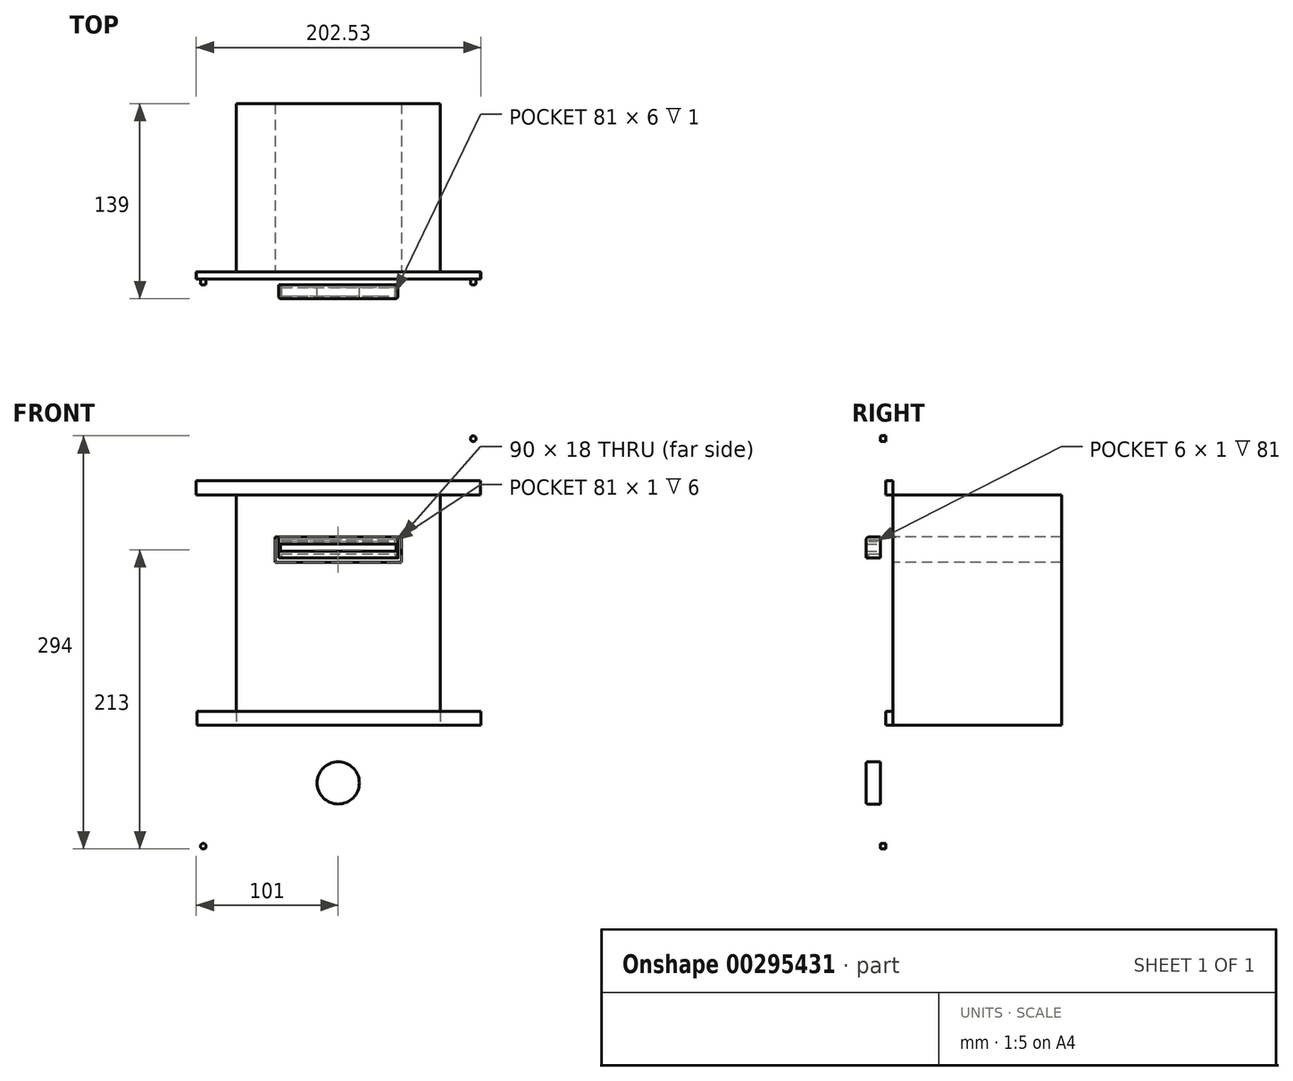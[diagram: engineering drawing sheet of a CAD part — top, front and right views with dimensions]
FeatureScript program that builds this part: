
annotation { "Feature Type Name" : "Feature", "Feature Type Description" : "" }
export const myFeature = defineFeature(function(context is Context, id is Id, definition is map)
    precondition{}
    {
        {
            var Q0;
            Q0=qCreatedBy(makeId("Front.planeOp"),FACE);
            var sketch = newSketch(context, id + "F0", { "sketchPlane" : qUnion([Q0])});
            skLineSegment(sketch, "E0.bottom", {"start": v(-143.29, 262) * mm, "end": v(58.71, 262) * mm});
            skLineSegment(sketch, "E0.top", {"start": v(-143.29, -38) * mm, "end": v(58.71, -38) * mm});
            skLineSegment(sketch, "E0.left", {"start": v(-143.29, 262) * mm, "end": v(-143.29, -38) * mm});
            skLineSegment(sketch, "E0.right", {"start": v(58.71, 262) * mm, "end": v(58.71, -38) * mm});
            skSolve(sketch);
        }
        {
            var Q0;
            Q0=makeQuery(id+"F0.imprint","IMPRINT",FACE,{"disambiguationData":[TD([[makeQuery(id+"F0.imprint","IMPRINT",EDGE,{"derivedFrom":sQuery(id+"F0.wireOp",EDGE,"E0.bottom")}),-1.0]])]});
            extrude(context, id + "F1", {"entities" : qUnion([Q0]), "depth" : 4 * mm});
        }
        {
            var Q0;
            Q0=makeQuery(id+"F1.opExtrude","CAP_FACE",FACE,{"disambiguationData":[OSD([sQuery(id+"F0.wireOp",EDGE,"E0.bottom"),sQuery(id+"F0.wireOp",EDGE,"E0.top"),sQuery(id+"F0.wireOp",EDGE,"E0.left"),sQuery(id+"F0.wireOp",EDGE,"E0.right")])],"isStart":false});
            var sketch = newSketch(context, id + "F2", { "sketchPlane" : qUnion([Q0])});
            skCircle(sketch, "E1", {"center": v(-138.29, 257) * mm, "radius": 2 * mm});
            skLineSegment(sketch, "E2", {"start": v(-143.29, 262) * mm, "end": v(-143.29, -38) * mm, "construction": true});
            skLineSegment(sketch, "E3", {"start": v(-143.29, 112) * mm, "end": v(-42.29, 112) * mm, "construction": true});
            skLineSegment(sketch, "E4", {"start": v(-42.29, 112) * mm, "end": v(-42.29, 262) * mm, "construction": true});
            skCircle(sketch, "E5.MirrorC", {"center": v(-138.29, -33) * mm, "radius": 2 * mm});
            skLineSegment(sketch, "E6.bottom", {"start": v(-83.29, 182) * mm, "end": v(-1.29, 182) * mm});
            skLineSegment(sketch, "E6.top", {"start": v(-83.29, 177) * mm, "end": v(-1.29, 177) * mm});
            skLineSegment(sketch, "E6.left", {"start": v(-83.29, 182) * mm, "end": v(-83.29, 177) * mm});
            skLineSegment(sketch, "E6.right", {"start": v(-1.29, 182) * mm, "end": v(-1.29, 177) * mm});
            skCircle(sketch, "E7.MirrorC", {"center": v(53.71, 257) * mm, "radius": 2 * mm});
            skCircle(sketch, "E8.MirrorC", {"center": v(53.71, -33) * mm, "radius": 2 * mm});
            skSolve(sketch);
        }
        {
            var Q0;
            Q0=makeQuery(id+"F2.imprint","IMPRINT",FACE,{"disambiguationData":[TD([[makeQuery(id+"F2.imprint","IMPRINT",EDGE,{"derivedFrom":sQuery(id+"F2.wireOp",EDGE,"f3714297-d91a-48a6-a239-89a6e6a1d6ad0.MirrorC")}),1.0]])]});
            var Q1;
            Q1=makeQuery(id+"F2.imprint","IMPRINT",FACE,{"disambiguationData":[TD([[makeQuery(id+"F2.imprint","IMPRINT",EDGE,{"derivedFrom":sQuery(id+"F2.wireOp",EDGE,"E5.MirrorC")}),-1.0]])]});
            var Q2;
            Q2=makeQuery(id+"F2.imprint","IMPRINT",FACE,{"disambiguationData":[TD([[makeQuery(id+"F2.imprint","IMPRINT",EDGE,{"derivedFrom":sQuery(id+"F2.wireOp",EDGE,"8d8d8ab8-7da3-4b74-95fe-22b7e39185220.MirrorC")}),-1.0]])]});
            var Q3;
            Q3=makeQuery(id+"F2.imprint","IMPRINT",FACE,{"disambiguationData":[TD([[makeQuery(id+"F2.imprint","IMPRINT",EDGE,{"derivedFrom":sQuery(id+"F2.wireOp",EDGE,"E1")}),1.0]])]});
            var Q4;
            Q4=makeQuery(id+"F2.imprint","IMPRINT",FACE,{"disambiguationData":[TD([[makeQuery(id+"F2.imprint","IMPRINT",EDGE,{"derivedFrom":sQuery(id+"F2.wireOp",EDGE,"E7.MirrorC")}),-1.0]])]});
            var Q5;
            Q5=makeQuery(id+"F2.imprint","IMPRINT",FACE,{"disambiguationData":[TD([[makeQuery(id+"F2.imprint","IMPRINT",EDGE,{"derivedFrom":sQuery(id+"F2.wireOp",EDGE,"E8.MirrorC")}),1.0]])]});
            extrude(context, id + "F3", {"entities" : qUnion([Q0, Q1, Q2, Q3, Q4, Q5]), "operationType" : NewBodyOperationType.REMOVE, "oppositeDirection" : true, "depth" : 5 * mm});
        }
        {
            var Q0;
            Q0=makeQuery(id+"F1.opExtrude","CAP_FACE",FACE,{"disambiguationData":[OSD([sQuery(id+"F0.wireOp",EDGE,"E0.bottom"),sQuery(id+"F0.wireOp",EDGE,"E0.top"),sQuery(id+"F0.wireOp",EDGE,"E0.left"),sQuery(id+"F0.wireOp",EDGE,"E0.right")])],"isStart":false});
            var sketch = newSketch(context, id + "F4", { "sketchPlane" : qUnion([Q0])});
            skLineSegment(sketch, "E9", {"start": v(-143.29, -38) * mm, "end": v(58.71, -38) * mm, "construction": true});
            skLineSegment(sketch, "E10", {"start": v(-42.29, -38) * mm, "end": v(-42.29, 12) * mm, "construction": true});
            skCircle(sketch, "E11", {"center": v(-42.29, 12) * mm, "radius": 15 * mm});
            skSolve(sketch);
        }
        {
            var Q0;
            Q0=makeQuery(id+"F4.imprint","IMPRINT",FACE,{"disambiguationData":[TD([[makeQuery(id+"F4.imprint","IMPRINT",EDGE,{"derivedFrom":sQuery(id+"F4.wireOp",EDGE,"E11")}),1.0]])]});
            extrude(context, id + "F5", {"entities" : qUnion([Q0]), "depth" : 10 * mm});
        }
        {
            var Q0;
            Q0=makeQuery(id+"F5.opExtrude","CAP_FACE",FACE,{"disambiguationData":[OSD([sQuery(id+"F4.wireOp",EDGE,"E11")])],"isStart":false});
            fillet(context, id + "F6", {"entities" : qUnion([Q0]), "radius" : 1 * mm, "tangentPropagation" : true, "allowEdgeOverflow" : false});
        }
        {
            var Q0;
            Q0=makeQuery(id+"F1.opExtrude","CAP_FACE",FACE,{"disambiguationData":[OSD([sQuery(id+"F0.wireOp",EDGE,"E0.bottom"),sQuery(id+"F0.wireOp",EDGE,"E0.top"),sQuery(id+"F0.wireOp",EDGE,"E0.left"),sQuery(id+"F0.wireOp",EDGE,"E0.right")])],"isStart":false});
            var sketch = newSketch(context, id + "F7", { "sketchPlane" : qUnion([Q0])});
            skLineSegment(sketch, "E12.bottom", {"start": v(-84.79, 187) * mm, "end": v(0.21, 187) * mm});
            skLineSegment(sketch, "E12.top", {"start": v(-84.79, 172) * mm, "end": v(0.21, 172) * mm});
            skLineSegment(sketch, "E12.left", {"start": v(-84.79, 187) * mm, "end": v(-84.79, 172) * mm});
            skLineSegment(sketch, "E12.right", {"start": v(0.21, 187) * mm, "end": v(0.21, 172) * mm});
            skSolve(sketch);
        }
        {
            var Q0;
            Q0=makeQuery(id+"F7.imprint","IMPRINT",FACE,{"disambiguationData":[TD([[makeQuery(id+"F7.imprint","IMPRINT",EDGE,{"derivedFrom":sQuery(id+"F7.wireOp",EDGE,"E12.bottom")}),-1.0]])]});
            extrude(context, id + "F8", {"entities" : qUnion([Q0]), "depth" : 10 * mm});
        }
        {
            var Q0;
            Q0=makeQuery(id+"F8.opExtrude","CAP_EDGE",EDGE,{"disambiguationData":[OSD([sQuery(id+"F7.wireOp",EDGE,"E12.left")])],"isStart":false});
            var Q1;
            Q1=makeQuery(id+"F8.opExtrude","CAP_EDGE",EDGE,{"disambiguationData":[OSD([sQuery(id+"F7.wireOp",EDGE,"E12.bottom")])],"isStart":false});
            var Q2;
            Q2=makeQuery(id+"F8.opExtrude","CAP_EDGE",EDGE,{"disambiguationData":[OSD([sQuery(id+"F7.wireOp",EDGE,"E12.right")])],"isStart":false});
            var Q3;
            Q3=makeQuery(id+"F8.opExtrude","SWEPT_EDGE",EDGE,{"disambiguationData":[OSD([sQuery(id+"F7.wireOp",EDGE,"E12.bottom"),sQuery(id+"F7.wireOp",EDGE,"E12.right")])]});
            var Q4;
            Q4=makeQuery(id+"F8.opExtrude","SWEPT_EDGE",EDGE,{"disambiguationData":[OSD([sQuery(id+"F7.wireOp",EDGE,"E12.bottom"),sQuery(id+"F7.wireOp",EDGE,"E12.left")])]});
            fillet(context, id + "F9", {"entities" : qUnion([Q0, Q1, Q2, Q3, Q4]), "radius" : 2 * mm, "tangentPropagation" : true, "allowEdgeOverflow" : false});
        }
        {
            var Q0;
            Q0=makeQuery(id+"F8.opExtrude","SWEPT_FACE",FACE,{"disambiguationData":[OSD([sQuery(id+"F7.wireOp",EDGE,"E12.top")])]});
            shell(context, id + "F10", {"entities" : qUnion([Q0]), "thickness" : 2 * mm});
        }
        {
            var Q0;
            {var subQ0=sQuery(id+"F7.wireOp",EDGE,"E12.right");var subQ1=sQuery(id+"F7.wireOp",EDGE,"E12.left");var subQ2=sQuery(id+"F7.wireOp",EDGE,"E12.top");var subQ3=sQuery(id+"F7.wireOp",EDGE,"E12.bottom");Q0=makeQuery(id+"F10.opShell","OFFSET_FACE",FACE,{"disambiguationData":[OSD([subQ3,subQ2,subQ1,subQ0]),TDD([makeQuery(id+"F8.opExtrude","CAP_FACE",FACE,{"disambiguationData":[OSD([subQ3,subQ2,subQ1,subQ0])],"isStart":true})])]});}
            var sketch = newSketch(context, id + "F11", { "sketchPlane" : qUnion([Q0])});
            skLineSegment(sketch, "E13.bottom", {"start": v(-82.79, 172) * mm, "end": v(-1.79, 172) * mm});
            skLineSegment(sketch, "E13.top", {"start": v(-82.79, 185) * mm, "end": v(-1.79, 185) * mm});
            skLineSegment(sketch, "E13.left", {"start": v(-82.79, 172) * mm, "end": v(-82.79, 185) * mm});
            skLineSegment(sketch, "E13.right", {"start": v(-1.79, 172) * mm, "end": v(-1.79, 185) * mm});
            skSolve(sketch);
        }
        {
            var Q0;
            Q0=makeQuery(id+"F11.imprint","IMPRINT",FACE,{"disambiguationData":[TD([[makeQuery(id+"F11.imprint","IMPRINT",EDGE,{"derivedFrom":sQuery(id+"F11.wireOp",EDGE,"E13.bottom")}),1.0]])]});
            extrude(context, id + "F12", {"entities" : qUnion([Q0]), "operationType" : NewBodyOperationType.REMOVE, "oppositeDirection" : true, "depth" : 10 * mm});
        }
        {
            var Q0;
            Q0=makeQuery(id+"F2.imprint","IMPRINT",FACE,{"disambiguationData":[TD([[makeQuery(id+"F2.imprint","IMPRINT",EDGE,{"derivedFrom":sQuery(id+"F2.wireOp",EDGE,"E6.bottom")}),-1.0]])]});
            extrude(context, id + "F13", {"entities" : qUnion([Q0]), "operationType" : NewBodyOperationType.REMOVE, "oppositeDirection" : true, "depth" : 25 * mm});
        }
        {
            var Q0;
            Q0=makeQuery(id+"F3.boolean.opBoolean","COPY",EDGE,{"derivedFrom":makeQuery(id+"F3.opExtrude","CAP_EDGE",EDGE,{"disambiguationData":[OSD([sQuery(id+"F2.wireOp",EDGE,"E1")])],"isStart":true})});
            var Q1;
            Q1=makeQuery(id+"F3.boolean.opBoolean","COPY",EDGE,{"derivedFrom":makeQuery(id+"F3.opExtrude","CAP_EDGE",EDGE,{"disambiguationData":[OSD([sQuery(id+"F2.wireOp",EDGE,"8d8d8ab8-7da3-4b74-95fe-22b7e39185220.MirrorC")])],"isStart":true})});
            var Q2;
            Q2=makeQuery(id+"F3.boolean.opBoolean","COPY",EDGE,{"derivedFrom":makeQuery(id+"F3.opExtrude","CAP_EDGE",EDGE,{"disambiguationData":[OSD([sQuery(id+"F2.wireOp",EDGE,"f3714297-d91a-48a6-a239-89a6e6a1d6ad0.MirrorC")])],"isStart":true})});
            var Q3;
            Q3=makeQuery(id+"F3.boolean.opBoolean","COPY",EDGE,{"derivedFrom":makeQuery(id+"F3.opExtrude","CAP_EDGE",EDGE,{"disambiguationData":[OSD([sQuery(id+"F2.wireOp",EDGE,"E5.MirrorC")])],"isStart":true})});
            var Q4;
            Q4=makeQuery(id+"F3.boolean.opBoolean","COPY",EDGE,{"derivedFrom":makeQuery(id+"F3.opExtrude","CAP_EDGE",EDGE,{"disambiguationData":[OSD([sQuery(id+"F2.wireOp",EDGE,"E8.MirrorC")])],"isStart":true})});
            var Q5;
            Q5=makeQuery(id+"F3.boolean.opBoolean","COPY",EDGE,{"derivedFrom":makeQuery(id+"F3.opExtrude","CAP_EDGE",EDGE,{"disambiguationData":[OSD([sQuery(id+"F2.wireOp",EDGE,"E7.MirrorC")])],"isStart":true})});
            fillet(context, id + "F14", {"entities" : qUnion([Q0, Q1, Q2, Q3, Q4, Q5]), "radius" : 1 * mm, "tangentPropagation" : true, "allowEdgeOverflow" : false});
        }
        {
            var Q0;
            Q0=makeQuery(id+"F0.imprint","IMPRINT",FACE,{"disambiguationData":[TD([[makeQuery(id+"F0.imprint","IMPRINT",EDGE,{"derivedFrom":sQuery(id+"F0.wireOp",EDGE,"E0.bottom")}),-1.0]])]});
            var sketch = newSketch(context, id + "F15", { "sketchPlane" : qUnion([Q0])});
            skLineSegment(sketch, "E14.bottom", {"start": v(58.71, 227) * mm, "end": v(-143.29, 227) * mm});
            skLineSegment(sketch, "E14.top", {"start": v(58.71, 217) * mm, "end": v(-143.29, 217) * mm});
            skLineSegment(sketch, "E14.left", {"start": v(58.71, 227) * mm, "end": v(58.71, 217) * mm});
            skLineSegment(sketch, "E14.right", {"start": v(-143.29, 227) * mm, "end": v(-143.29, 217) * mm});
            skLineSegment(sketch, "E15.bottom", {"start": v(59.24, 63) * mm, "end": v(-142.76, 63) * mm});
            skLineSegment(sketch, "E15.top", {"start": v(59.24, 53) * mm, "end": v(-142.76, 53) * mm});
            skLineSegment(sketch, "E15.left", {"start": v(59.24, 63) * mm, "end": v(59.24, 53) * mm});
            skLineSegment(sketch, "E15.right", {"start": v(-142.76, 63) * mm, "end": v(-142.76, 53) * mm});
            skSolve(sketch);
        }
        {
            var Q0;
            Q0 = qSketchRegion(id + "F15", true);
            extrude(context, id + "F16", {"entities" : qUnion([Q0]), "oppositeDirection" : true, "depth" : 5 * mm});
        }
        {
            var Q0;
            Q0=makeQuery(id+"F16.opExtrude","CAP_FACE",FACE,{"disambiguationData":[OSD([sQuery(id+"F15.wireOp",EDGE,"E14.bottom"),sQuery(id+"F15.wireOp",EDGE,"E14.top"),sQuery(id+"F15.wireOp",EDGE,"E14.left"),sQuery(id+"F15.wireOp",EDGE,"E14.right")])],"isStart":false});
            var sketch = newSketch(context, id + "F17", { "sketchPlane" : qUnion([Q0])});
            skLineSegment(sketch, "E16.bottom", {"start": v(-30.21, 227) * mm, "end": v(114.79, 227) * mm});
            skLineSegment(sketch, "E16.top", {"start": v(-30.21, 53) * mm, "end": v(114.79, 53) * mm});
            skLineSegment(sketch, "E16.left", {"start": v(-30.21, 227) * mm, "end": v(-30.21, 53) * mm});
            skLineSegment(sketch, "E16.right", {"start": v(114.79, 227) * mm, "end": v(114.79, 53) * mm});
            skLineSegment(sketch, "E17.bottom", {"start": v(87.29, 187) * mm, "end": v(-2.71, 187) * mm});
            skLineSegment(sketch, "E17.top", {"start": v(87.29, 169) * mm, "end": v(-2.71, 169) * mm});
            skLineSegment(sketch, "E17.left", {"start": v(87.29, 187) * mm, "end": v(87.29, 169) * mm});
            skLineSegment(sketch, "E17.right", {"start": v(-2.71, 187) * mm, "end": v(-2.71, 169) * mm});
            skSolve(sketch);
        }
        {
            var Q0;
            {var subQ0=sQuery(id+"F17.wireOp",EDGE,"E16.top");Q0=makeQuery(id+"F17.imprint","IMPRINT",FACE,{"disambiguationData":[TD([[makeQuery(id+"F17.imprint","IMPRINT",EDGE,{"derivedFrom":subQ0}),1.0]])]});}
            extrude(context, id + "F18", {"entities" : qUnion([Q0]), "depth" : 120 * mm});
        }
    });
